# Revit family: Lav-Corian-European-Quiet-7110
name_source: partatom
category: Plumbing Fixtures
revit_build: Autodesk Revit 2015 (Build: 20140606_1530(x64)
units: mm (PartAtom-declared; Revit-internal decimal feet)

## types (1)
- 7110
    CWFU = 0
    Cost = 0 $
    Default Elevation = 1219 mm
    Depth = 130 mm  [stored 0.426509 ft]
    Description = Bathroom Basin Europe Specification
    Finish = Solid Surface Sink - DuPont - Designer White
    HWFU = 0
    Interior Depth = 110 mm  [stored 0.360892 ft]
    Interior Length = 300 mm
    Interior Width = 450 mm  [stored 1.47638 ft]
    Length = 350 mm  [stored 1.14829 ft]
    Manufacturer = DuPont
    Model = Quiet 7110
    Product Page URL = http://www.corian.uk
    Sink Colors Available = Designer White, Glacier White
    URL = http://www.corian.uk
    Version = 2015 - v1.0b
    WFU = 0
    Width = 500 mm  [stored 1.64042 ft]

note: [stored X ft] marks values corroborated as IEEE doubles in the binary element streams (Revit-internal decimal feet)

## geometry (parser evidence)
native form markers: Sweep x5
no freeform markers — native parametric forms only
